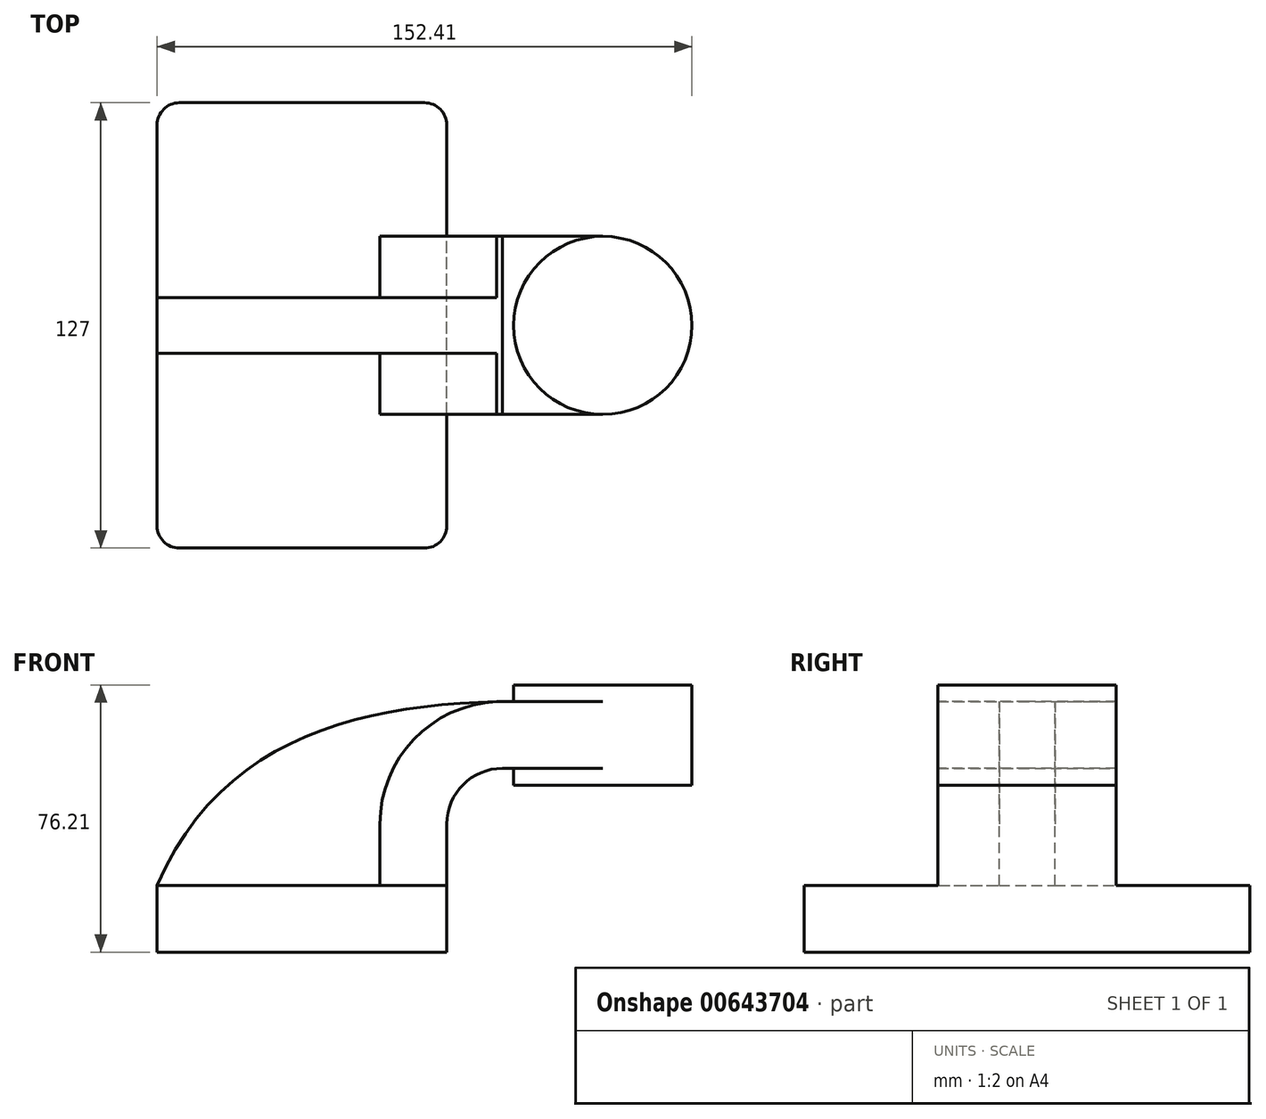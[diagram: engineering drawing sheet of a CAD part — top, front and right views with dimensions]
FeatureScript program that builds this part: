
annotation { "Feature Type Name" : "Feature", "Feature Type Description" : "" }
export const myFeature = defineFeature(function(context is Context, id is Id, definition is map)
    precondition{}
    {
        {
            var Q0;
            Q0=qCreatedBy(makeId("Front.planeOp"),FACE);
            var sketch = newSketch(context, id + "F0", { "sketchPlane" : qUnion([Q0])});
            skLineSegment(sketch, "E0.bottom", {"start": v(41.28, 9.53) * mm, "end": v(-41.28, 9.53) * mm});
            skLineSegment(sketch, "E0.top", {"start": v(41.28, -9.52) * mm, "end": v(-41.28, -9.53) * mm});
            skLineSegment(sketch, "E0.left", {"start": v(41.28, 9.53) * mm, "end": v(41.28, -9.52) * mm});
            skLineSegment(sketch, "E0.right", {"start": v(-41.28, 9.53) * mm, "end": v(-41.28, -9.53) * mm});
            skPoint(sketch, "E0.middle", {"position": v(0, 0) * mm});
            skLineSegment(sketch, "E1.bottom", {"start": v(60.33, 38.1) * mm, "end": v(111.13, 38.1) * mm});
            skLineSegment(sketch, "E1.top", {"start": v(60.32, 66.68) * mm, "end": v(111.13, 66.68) * mm});
            skLineSegment(sketch, "E1.left", {"start": v(60.33, 38.1) * mm, "end": v(60.32, 66.67) * mm});
            skLineSegment(sketch, "E1.right", {"start": v(111.13, 38.1) * mm, "end": v(111.13, 66.67) * mm});
            skPoint(sketch, "E1.middle", {"position": v(85.73, 52.39) * mm});
            skLineSegment(sketch, "E2", {"start": v(41.28, 9.53) * mm, "end": v(41.28, 27) * mm});
            skArc(sketch, "E3", {"start": v(41.27, 27) * mm, "mid": v(45.92, 38.23) * mm, "end": v(57.15, 42.88) * mm});
            skLineSegment(sketch, "E4", {"start": v(57.15, 42.88) * mm, "end": v(85.72, 42.88) * mm});
            skLineSegment(sketch, "E5.0", {"start": v(57.15, 61.93) * mm, "end": v(85.72, 61.93) * mm});
            skArc(sketch, "E5.1", {"start": v(22.23, 27) * mm, "mid": v(32.45, 51.7) * mm, "end": v(57.15, 61.93) * mm});
            skLineSegment(sketch, "E5.2", {"start": v(22.22, 9.53) * mm, "end": v(22.22, 27) * mm});
            skLineSegment(sketch, "E6", {"start": v(85.72, 38.1) * mm, "end": v(85.72, 66.68) * mm});
            skFitSpline(sketch, "E7", {"points": [v(-41.28, 9.53) * mm, v(57.15, 61.93) * mm], "startDerivative": vector(54.75, 126.91) * mm, "endDerivative": vector(122.11, 2.55) * mm});
            skSolve(sketch);
        }
        {
            var Q0;
            Q0=makeQuery(id+"F0.imprint","IMPRINT",FACE,{"disambiguationData":[TD([[makeQuery(id+"F0.imprint","IMPRINT",EDGE,{"derivedFrom":sQuery(id+"F0.wireOp",EDGE,"E0.top")}),-1.0]])]});
            extrude(context, id + "F1", {"entities" : qUnion([Q0]), "endBound" : BoundingType.SYMMETRIC, "depth" : 127 * mm, "offsetDistance" : 25.4 * mm});
        }
        {
            var Q0;
            {var subQ0=sQuery(id+"F0.wireOp",EDGE,"E4");var subQ1=sQuery(id+"F0.wireOp",EDGE,"E1.left");var subQ2=makeQuery(id+"F0.imprint","INTERSECT",VERTEX,{"derivedFrom":[subQ1,subQ0]});Q0=makeQuery(id+"F0.imprint","IMPRINT",FACE,{"disambiguationData":[TD([[makeQuery(id+"F0.imprint","IMPRINT",EDGE,{"disambiguationData":[TD([[subQ2,-1.0]])],"derivedFrom":subQ1}),-1.0]])]});}
            var Q1;
            {var subQ1=sQuery(id+"F0.wireOp",EDGE,"E2");Q1=makeQuery(id+"F0.imprint","IMPRINT",FACE,{"disambiguationData":[TD([[makeQuery(id+"F0.imprint","IMPRINT",EDGE,{"derivedFrom":subQ1}),1.0]])]});}
            extrude(context, id + "F2", {"entities" : qUnion([Q0, Q1]), "operationType" : NewBodyOperationType.ADD, "endBound" : BoundingType.SYMMETRIC, "depth" : 50.8 * mm, "offsetDistance" : 25.4 * mm});
        }
        {
            var Q0;
            {var subQ3=sQuery(id+"F0.wireOp",EDGE,"E5.2");Q0=makeQuery(id+"F0.imprint","IMPRINT",FACE,{"disambiguationData":[TD([[makeQuery(id+"F0.imprint","IMPRINT",EDGE,{"derivedFrom":subQ3}),1.0]])]});}
            extrude(context, id + "F3", {"entities" : qUnion([Q0]), "operationType" : NewBodyOperationType.ADD, "endBound" : BoundingType.SYMMETRIC, "depth" : 15.88 * mm, "offsetDistance" : 25.4 * mm});
        }
        {
            var Q0;
            {var subQ4=sQuery(id+"F0.wireOp",EDGE,"E1.right");Q0=makeQuery(id+"F0.imprint","IMPRINT",FACE,{"disambiguationData":[TD([[makeQuery(id+"F0.imprint","IMPRINT",EDGE,{"derivedFrom":subQ4}),1.0]])]});}
            var Q1;
            Q1=sQuery(id+"F0.wireOp",EDGE,"E6");
            revolve(context, id + "F4", {"operationType" : NewBodyOperationType.ADD, "entities" : qUnion([Q0]), "axis" : qUnion([Q1]), "revolveType" : RevolveType.FULL});
        }
        {
            var Q0;
            Q0=makeQuery(id+"F1.opExtrude","CAP_EDGE",EDGE,{"disambiguationData":[OSD([sQuery(id+"F0.wireOp",EDGE,"E0.right")])],"isStart":false});
            var Q1;
            Q1=makeQuery(id+"F1.opExtrude","CAP_EDGE",EDGE,{"disambiguationData":[OSD([sQuery(id+"F0.wireOp",EDGE,"E0.left")])],"isStart":false});
            var Q2;
            Q2=makeQuery(id+"F1.opExtrude","CAP_EDGE",EDGE,{"disambiguationData":[OSD([sQuery(id+"F0.wireOp",EDGE,"E0.right")])],"isStart":true});
            var Q3;
            Q3=makeQuery(id+"F1.opExtrude","CAP_EDGE",EDGE,{"disambiguationData":[OSD([sQuery(id+"F0.wireOp",EDGE,"E0.left")])],"isStart":true});
            fillet(context, id + "F5", {"entities" : qUnion([Q0, Q1, Q2, Q3]), "radius" : 6.35 * mm, "tangentPropagation" : true, "allowEdgeOverflow" : false});
        }
    });
